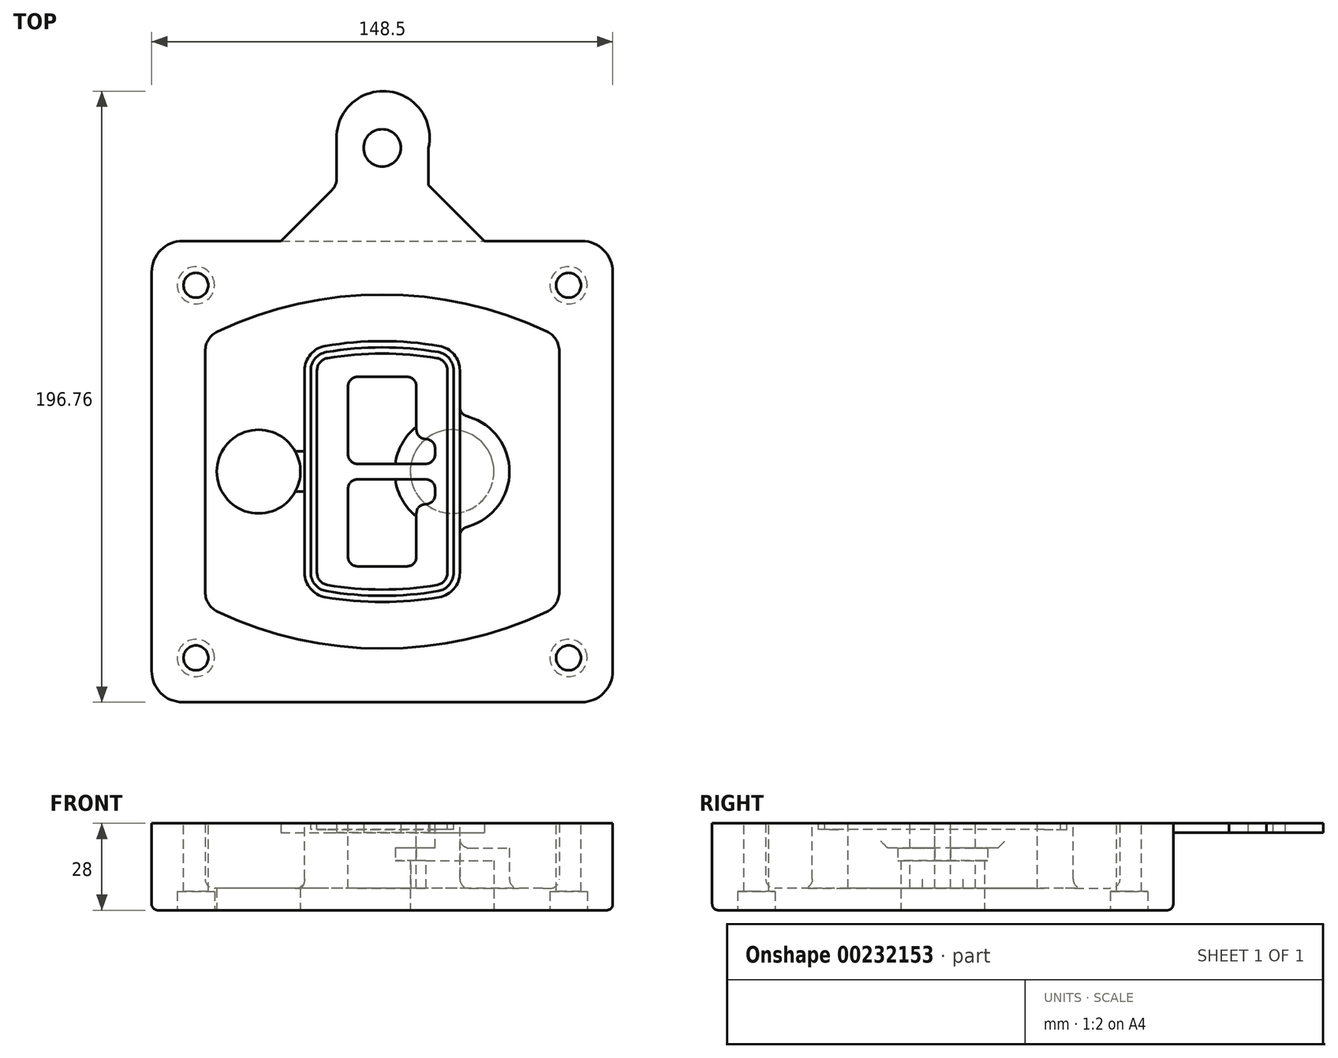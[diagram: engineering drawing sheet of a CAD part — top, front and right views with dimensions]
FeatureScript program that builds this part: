
annotation { "Feature Type Name" : "Feature", "Feature Type Description" : "" }
export const myFeature = defineFeature(function(context is Context, id is Id, definition is map)
    precondition{}
    {
        {
            var Q0;
            Q0=qCreatedBy(makeId("Top.planeOp"),FACE);
            var sketch = newSketch(context, id + "F0", { "sketchPlane" : qUnion([Q0])});
            skPoint(sketch, "E0.rect.middle", {"position": v(0, 0) * mm});
            skLineSegment(sketch, "E1.bottom", {"start": v(-64.25, -74.25) * mm, "end": v(64.25, -74.25) * mm});
            skLineSegment(sketch, "E1.top", {"start": v(-64.25, 74.25) * mm, "end": v(64.25, 74.25) * mm});
            skLineSegment(sketch, "E1.left", {"start": v(-74.25, -64.25) * mm, "end": v(-74.25, 64.25) * mm});
            skLineSegment(sketch, "E1.right", {"start": v(74.25, -64.25) * mm, "end": v(74.25, 64.25) * mm});
            skLineSegment(sketch, "E2", {"start": v(-74.25, 74.25) * mm, "end": v(74.25, -74.25) * mm, "construction": true});
            skLineSegment(sketch, "E3", {"start": v(74.25, 74.25) * mm, "end": v(-74.25, -74.25) * mm, "construction": true});
            skCircle(sketch, "E4", {"center": v(-60, 60) * mm, "radius": 4 * mm});
            skCircle(sketch, "E5", {"center": v(60, 60) * mm, "radius": 4 * mm});
            skCircle(sketch, "E6", {"center": v(60, -60) * mm, "radius": 4 * mm});
            skCircle(sketch, "E7", {"center": v(-60, -60) * mm, "radius": 4 * mm});
            skLineSegment(sketch, "E8", {"start": v(-60, 60) * mm, "end": v(60, 60) * mm, "construction": true});
            skLineSegment(sketch, "E9", {"start": v(60, 60) * mm, "end": v(60, -60) * mm, "construction": true});
            skLineSegment(sketch, "E10", {"start": v(60, -60) * mm, "end": v(-60, -60) * mm, "construction": true});
            skLineSegment(sketch, "E11", {"start": v(-60, -60) * mm, "end": v(-60, 60) * mm, "construction": true});
            skLineSegment(sketch, "E12", {"start": v(-60, 38.83) * mm, "end": v(-60, -38.83) * mm});
            skLineSegment(sketch, "E13", {"start": v(60, 38.83) * mm, "end": v(60, -38.83) * mm});
            skArc(sketch, "E14", {"start": v(54.26, 47.88) * mm, "mid": v(0, 60) * mm, "end": v(-54.26, 47.88) * mm});
            skArc(sketch, "E15", {"start": v(-54.26, -47.88) * mm, "mid": v(0, -60) * mm, "end": v(54.26, -47.88) * mm});
            skLineSegment(sketch, "E16", {"start": v(-60, 0) * mm, "end": v(60, 0) * mm, "construction": true});
            skPoint(sketch, "E17.visualSharp", {"position": v(-60, -45) * mm});
            skArc(sketch, "E17.filletArc", {"start": v(-60, -38.83) * mm, "mid": v(-58.44, -44.2) * mm, "end": v(-54.26, -47.88) * mm});
            skPoint(sketch, "E18.visualSharp", {"position": v(-60, 45) * mm});
            skArc(sketch, "E18.filletArc", {"start": v(-54.26, 47.88) * mm, "mid": v(-58.44, 44.2) * mm, "end": v(-60, 38.83) * mm});
            skPoint(sketch, "E19.visualSharp", {"position": v(60, 45) * mm});
            skArc(sketch, "E19.filletArc", {"start": v(60, 38.83) * mm, "mid": v(58.44, 44.2) * mm, "end": v(54.26, 47.88) * mm});
            skPoint(sketch, "E20.visualSharp", {"position": v(60, -45) * mm});
            skArc(sketch, "E20.filletArc", {"start": v(54.26, -47.88) * mm, "mid": v(58.44, -44.2) * mm, "end": v(60, -38.83) * mm});
            skPoint(sketch, "E21.visualSharp", {"position": v(-74.25, 74.25) * mm});
            skArc(sketch, "E21.filletArc", {"start": v(-64.25, 74.25) * mm, "mid": v(-71.32, 71.32) * mm, "end": v(-74.25, 64.25) * mm});
            skPoint(sketch, "E22.visualSharp", {"position": v(74.25, 74.25) * mm});
            skArc(sketch, "E22.filletArc", {"start": v(74.25, 64.25) * mm, "mid": v(71.32, 71.32) * mm, "end": v(64.25, 74.25) * mm});
            skPoint(sketch, "E23.visualSharp", {"position": v(74.25, -74.25) * mm});
            skArc(sketch, "E23.filletArc", {"start": v(64.25, -74.25) * mm, "mid": v(71.32, -71.32) * mm, "end": v(74.25, -64.25) * mm});
            skPoint(sketch, "E24.visualSharp", {"position": v(-74.25, -74.25) * mm});
            skArc(sketch, "E24.filletArc", {"start": v(-74.25, -64.25) * mm, "mid": v(-71.32, -71.32) * mm, "end": v(-64.25, -74.25) * mm});
            skArc(sketch, "E25.0", {"start": v(57, 38.83) * mm, "mid": v(55.9, 42.58) * mm, "end": v(52.98, 45.17) * mm});
            skLineSegment(sketch, "E25.1", {"start": v(57, 38.83) * mm, "end": v(57, -38.83) * mm});
            skArc(sketch, "E25.2", {"start": v(52.98, -45.17) * mm, "mid": v(55.9, -42.58) * mm, "end": v(57, -38.83) * mm});
            skArc(sketch, "E25.3", {"start": v(-52.98, -45.17) * mm, "mid": v(0, -57) * mm, "end": v(52.98, -45.17) * mm});
            skArc(sketch, "E25.4", {"start": v(-57, -38.83) * mm, "mid": v(-55.9, -42.58) * mm, "end": v(-52.98, -45.17) * mm});
            skArc(sketch, "E25.5", {"start": v(52.98, 45.17) * mm, "mid": v(0, 57) * mm, "end": v(-52.98, 45.17) * mm});
            skLineSegment(sketch, "E25.6", {"start": v(-57, 38.83) * mm, "end": v(-57, -38.83) * mm});
            skArc(sketch, "E25.7", {"start": v(-52.98, 45.17) * mm, "mid": v(-55.9, 42.58) * mm, "end": v(-57, 38.83) * mm});
            skArc(sketch, "E26.0", {"start": v(-55.96, 51.5) * mm, "mid": v(-61.82, 46.33) * mm, "end": v(-64, 38.83) * mm});
            skArc(sketch, "E26.1", {"start": v(55.96, 51.5) * mm, "mid": v(0, 64) * mm, "end": v(-55.96, 51.5) * mm});
            skArc(sketch, "E26.2", {"start": v(64, 38.83) * mm, "mid": v(61.82, 46.33) * mm, "end": v(55.96, 51.5) * mm});
            skLineSegment(sketch, "E26.3", {"start": v(64, 38.83) * mm, "end": v(64, -38.83) * mm});
            skArc(sketch, "E26.4", {"start": v(55.96, -51.5) * mm, "mid": v(61.82, -46.33) * mm, "end": v(64, -38.83) * mm});
            skLineSegment(sketch, "E26.5", {"start": v(-64, 38.83) * mm, "end": v(-64, -38.83) * mm});
            skArc(sketch, "E26.6", {"start": v(-55.96, -51.5) * mm, "mid": v(0, -64) * mm, "end": v(55.96, -51.5) * mm});
            skArc(sketch, "E26.7", {"start": v(-64, -38.83) * mm, "mid": v(-61.82, -46.33) * mm, "end": v(-55.96, -51.5) * mm});
            skSolve(sketch);
        }
        {
            var Q0;
            Q0=makeQuery(id+"F0.imprint","IMPRINT",FACE,{"disambiguationData":[TD([[makeQuery(id+"F0.imprint","IMPRINT",EDGE,{"derivedFrom":sQuery(id+"F0.wireOp",EDGE,"E1.bottom")}),1.0]])]});
            var Q1;
            Q1=makeQuery(id+"F0.imprint","IMPRINT",FACE,{"disambiguationData":[TD([[makeQuery(id+"F0.imprint","IMPRINT",EDGE,{"derivedFrom":sQuery(id+"F0.wireOp",EDGE,"E12")}),1.0]])]});
            var Q2;
            Q2=makeQuery(id+"F0.imprint","IMPRINT",FACE,{"disambiguationData":[TD([[makeQuery(id+"F0.imprint","IMPRINT",EDGE,{"derivedFrom":sQuery(id+"F0.wireOp",EDGE,"E25.0")}),1.0]])]});
            var Q3;
            Q3=makeQuery(id+"F0.imprint","IMPRINT",FACE,{"disambiguationData":[TD([[makeQuery(id+"F0.imprint","IMPRINT",EDGE,{"derivedFrom":sQuery(id+"F0.wireOp",EDGE,"E12")}),-1.0]])]});
            extrude(context, id + "F1", {"entities" : qUnion([Q0, Q1, Q2, Q3]), "oppositeDirection" : true, "depth" : 25 * mm});
        }
        {
            var Q0;
            Q0=makeQuery(id+"F0.imprint","IMPRINT",FACE,{"disambiguationData":[TD([[makeQuery(id+"F0.imprint","IMPRINT",EDGE,{"derivedFrom":sQuery(id+"F0.wireOp",EDGE,"E12")}),1.0]])]});
            extrude(context, id + "F2", {"entities" : qUnion([Q0]), "operationType" : NewBodyOperationType.ADD, "depth" : 3 * mm});
        }
        {
            var Q0;
            Q0=makeQuery(id+"F0.imprint","IMPRINT",FACE,{"disambiguationData":[TD([[makeQuery(id+"F0.imprint","IMPRINT",EDGE,{"derivedFrom":sQuery(id+"F0.wireOp",EDGE,"E25.0")}),1.0]])]});
            extrude(context, id + "F3", {"entities" : qUnion([Q0]), "operationType" : NewBodyOperationType.REMOVE, "oppositeDirection" : true, "depth" : 18 * mm});
        }
        {
            var Q0;
            Q0=makeQuery(id+"F2.opExtrude","CAP_FACE",FACE,{"disambiguationData":[OSD([sQuery(id+"F0.wireOp",EDGE,"E12"),sQuery(id+"F0.wireOp",EDGE,"E13"),sQuery(id+"F0.wireOp",EDGE,"E14"),sQuery(id+"F0.wireOp",EDGE,"E15"),sQuery(id+"F0.wireOp",EDGE,"E17.filletArc"),sQuery(id+"F0.wireOp",EDGE,"E18.filletArc"),sQuery(id+"F0.wireOp",EDGE,"E19.filletArc"),sQuery(id+"F0.wireOp",EDGE,"E20.filletArc"),sQuery(id+"F0.wireOp",EDGE,"E25.0"),sQuery(id+"F0.wireOp",EDGE,"E25.1"),sQuery(id+"F0.wireOp",EDGE,"E25.2"),sQuery(id+"F0.wireOp",EDGE,"E25.3"),sQuery(id+"F0.wireOp",EDGE,"E25.4"),sQuery(id+"F0.wireOp",EDGE,"E25.5"),sQuery(id+"F0.wireOp",EDGE,"E25.6"),sQuery(id+"F0.wireOp",EDGE,"E25.7")])],"isStart":false});
            var sketch = newSketch(context, id + "F4", { "sketchPlane" : qUnion([Q0])});
            skArc(sketch, "E27.0", {"start": v(-18.34, -40.45) * mm, "mid": v(0, -42) * mm, "end": v(18.34, -40.45) * mm});
            skArc(sketch, "E28.0", {"start": v(18.34, 40.45) * mm, "mid": v(0, 42) * mm, "end": v(-18.34, 40.45) * mm});
            skLineSegment(sketch, "E29", {"start": v(-25, 32.57) * mm, "end": v(-25, -32.57) * mm});
            skLineSegment(sketch, "E30", {"start": v(25, 32.57) * mm, "end": v(25, -32.57) * mm});
            skLineSegment(sketch, "E31", {"start": v(-25, 39.1) * mm, "end": v(25, 39.1) * mm, "construction": true});
            skLineSegment(sketch, "E32", {"start": v(-25, -39.1) * mm, "end": v(25, -39.1) * mm, "construction": true});
            skPoint(sketch, "E33.visualSharp", {"position": v(-25, 39.1) * mm});
            skArc(sketch, "E33.filletArc", {"start": v(-18.34, 40.45) * mm, "mid": v(-23.11, 37.73) * mm, "end": v(-25, 32.57) * mm});
            skPoint(sketch, "E34.visualSharp", {"position": v(25, 39.1) * mm});
            skArc(sketch, "E34.filletArc", {"start": v(25, 32.57) * mm, "mid": v(23.11, 37.73) * mm, "end": v(18.34, 40.45) * mm});
            skPoint(sketch, "E35.visualSharp", {"position": v(25, -39.1) * mm});
            skArc(sketch, "E35.filletArc", {"start": v(18.34, -40.45) * mm, "mid": v(23.11, -37.73) * mm, "end": v(25, -32.57) * mm});
            skPoint(sketch, "E36.visualSharp", {"position": v(-25, -39.1) * mm});
            skArc(sketch, "E36.filletArc", {"start": v(-25, -32.57) * mm, "mid": v(-23.11, -37.73) * mm, "end": v(-18.34, -40.45) * mm});
            skArc(sketch, "E37.0", {"start": v(52.98, 45.17) * mm, "mid": v(0, 57) * mm, "end": v(-52.98, 45.17) * mm});
            skArc(sketch, "E37.1", {"start": v(-52.98, 45.17) * mm, "mid": v(-55.9, 42.58) * mm, "end": v(-57, 38.83) * mm});
            skLineSegment(sketch, "E37.2", {"start": v(-57, 38.83) * mm, "end": v(-57, -38.83) * mm});
            skArc(sketch, "E37.3", {"start": v(-57, -38.83) * mm, "mid": v(-55.9, -42.58) * mm, "end": v(-52.98, -45.17) * mm});
            skArc(sketch, "E37.4", {"start": v(-52.98, -45.17) * mm, "mid": v(0, -57) * mm, "end": v(52.98, -45.17) * mm});
            skArc(sketch, "E37.5", {"start": v(52.98, -45.17) * mm, "mid": v(55.9, -42.58) * mm, "end": v(57, -38.83) * mm});
            skLineSegment(sketch, "E37.6", {"start": v(57, 38.83) * mm, "end": v(57, -38.83) * mm});
            skArc(sketch, "E37.7", {"start": v(57, 38.83) * mm, "mid": v(55.9, 42.58) * mm, "end": v(52.98, 45.17) * mm});
            skLineSegment(sketch, "E38.0", {"start": v(23, 32.57) * mm, "end": v(23, -32.57) * mm});
            skArc(sketch, "E38.1", {"start": v(18, -38.48) * mm, "mid": v(21.58, -36.44) * mm, "end": v(23, -32.57) * mm});
            skArc(sketch, "E38.2", {"start": v(-18, -38.48) * mm, "mid": v(0, -40) * mm, "end": v(18, -38.48) * mm});
            skArc(sketch, "E38.3", {"start": v(-23, -32.57) * mm, "mid": v(-21.58, -36.44) * mm, "end": v(-18, -38.48) * mm});
            skLineSegment(sketch, "E38.4", {"start": v(-23, 32.57) * mm, "end": v(-23, -32.57) * mm});
            skArc(sketch, "E38.5", {"start": v(23, 32.57) * mm, "mid": v(21.58, 36.44) * mm, "end": v(18, 38.48) * mm});
            skArc(sketch, "E38.6", {"start": v(-18, 38.48) * mm, "mid": v(-21.58, 36.44) * mm, "end": v(-23, 32.57) * mm});
            skArc(sketch, "E38.7", {"start": v(18, 38.48) * mm, "mid": v(0, 40) * mm, "end": v(-18, 38.48) * mm});
            skArc(sketch, "E39.0", {"start": v(21, 32.57) * mm, "mid": v(20.06, 35.15) * mm, "end": v(17.67, 36.5) * mm});
            skLineSegment(sketch, "E39.1", {"start": v(21, 32.57) * mm, "end": v(21, -32.57) * mm});
            skArc(sketch, "E39.2", {"start": v(17.67, -36.5) * mm, "mid": v(20.06, -35.15) * mm, "end": v(21, -32.57) * mm});
            skArc(sketch, "E39.3", {"start": v(-17.67, -36.5) * mm, "mid": v(0, -38) * mm, "end": v(17.67, -36.5) * mm});
            skArc(sketch, "E39.4", {"start": v(-21, -32.57) * mm, "mid": v(-20.06, -35.15) * mm, "end": v(-17.67, -36.5) * mm});
            skArc(sketch, "E39.5", {"start": v(17.67, 36.5) * mm, "mid": v(0, 38) * mm, "end": v(-17.67, 36.5) * mm});
            skLineSegment(sketch, "E39.6", {"start": v(-21, 32.57) * mm, "end": v(-21, -32.57) * mm});
            skArc(sketch, "E39.7", {"start": v(-17.67, 36.5) * mm, "mid": v(-20.06, 35.15) * mm, "end": v(-21, 32.57) * mm});
            skLineSegment(sketch, "E40", {"start": v(-25, 0) * mm, "end": v(25, 0) * mm, "construction": true});
            skLineSegment(sketch, "E41", {"start": v(-11, 5.5) * mm, "end": v(-11, 27.5) * mm});
            skLineSegment(sketch, "E42", {"start": v(-8, 30.5) * mm, "end": v(8, 30.5) * mm});
            skLineSegment(sketch, "E43", {"start": v(11, 27.5) * mm, "end": v(11, 13.5) * mm});
            skLineSegment(sketch, "E44", {"start": v(14, 10.5) * mm, "end": v(14, 10.5) * mm});
            skLineSegment(sketch, "E45", {"start": v(17, 7.5) * mm, "end": v(17, 5.5) * mm});
            skLineSegment(sketch, "E46", {"start": v(14, 2.5) * mm, "end": v(-8, 2.5) * mm});
            skPoint(sketch, "E47.visualSharp", {"position": v(-11, 30.5) * mm});
            skArc(sketch, "E47.filletArc", {"start": v(-8, 30.5) * mm, "mid": v(-10.12, 29.62) * mm, "end": v(-11, 27.5) * mm});
            skPoint(sketch, "E48.visualSharp", {"position": v(11, 30.5) * mm});
            skArc(sketch, "E48.filletArc", {"start": v(11, 27.5) * mm, "mid": v(10.12, 29.62) * mm, "end": v(8, 30.5) * mm});
            skPoint(sketch, "E49.visualSharp", {"position": v(11, 10.5) * mm});
            skArc(sketch, "E49.filletArc", {"start": v(11, 13.5) * mm, "mid": v(11.88, 11.38) * mm, "end": v(14, 10.5) * mm});
            skPoint(sketch, "E50.visualSharp", {"position": v(17, 10.5) * mm});
            skArc(sketch, "E50.filletArc", {"start": v(17, 7.5) * mm, "mid": v(16.12, 9.62) * mm, "end": v(14, 10.5) * mm});
            skPoint(sketch, "E51.visualSharp", {"position": v(17, 2.5) * mm});
            skArc(sketch, "E51.filletArc", {"start": v(14, 2.5) * mm, "mid": v(16.12, 3.38) * mm, "end": v(17, 5.5) * mm});
            skPoint(sketch, "E52.visualSharp", {"position": v(-11, 2.5) * mm});
            skArc(sketch, "E52.filletArc", {"start": v(-11, 5.5) * mm, "mid": v(-10.12, 3.38) * mm, "end": v(-8, 2.5) * mm});
            skLineSegment(sketch, "E53.0.MirrorCS", {"start": v(14, -2.5) * mm, "end": v(-8, -2.5) * mm});
            skArc(sketch, "E54.0.MirrorCS", {"start": v(-11, -5.5) * mm, "mid": v(-10.12, -3.38) * mm, "end": v(-8, -2.5) * mm});
            skLineSegment(sketch, "E55.0.MirrorCS", {"start": v(-11, -5.5) * mm, "end": v(-11, -27.5) * mm});
            skArc(sketch, "E56.0.MirrorCS", {"start": v(-8, -30.5) * mm, "mid": v(-10.12, -29.62) * mm, "end": v(-11, -27.5) * mm});
            skLineSegment(sketch, "E57.0.MirrorCS", {"start": v(-8, -30.5) * mm, "end": v(8, -30.5) * mm});
            skArc(sketch, "E58.0.MirrorCS", {"start": v(11, -27.5) * mm, "mid": v(10.12, -29.62) * mm, "end": v(8, -30.5) * mm});
            skLineSegment(sketch, "E59.0.MirrorCS", {"start": v(11, -27.5) * mm, "end": v(11, -13.5) * mm});
            skArc(sketch, "E60.0.MirrorCS", {"start": v(11, -13.5) * mm, "mid": v(11.88, -11.38) * mm, "end": v(14, -10.5) * mm});
            skArc(sketch, "E61.0.MirrorCS", {"start": v(17, -7.5) * mm, "mid": v(16.12, -9.62) * mm, "end": v(14, -10.5) * mm});
            skLineSegment(sketch, "E62.0.MirrorCS", {"start": v(17, -7.5) * mm, "end": v(17, -5.5) * mm});
            skArc(sketch, "E63.0.MirrorCS", {"start": v(14, -2.5) * mm, "mid": v(16.12, -3.38) * mm, "end": v(17, -5.5) * mm});
            skSolve(sketch);
        }
        {
            var Q0;
            Q0=makeQuery(id+"F4.imprint","IMPRINT",FACE,{"disambiguationData":[TD([[makeQuery(id+"F4.imprint","IMPRINT",EDGE,{"derivedFrom":sQuery(id+"F4.wireOp",EDGE,"E27.0")}),1.0]])]});
            var Q1;
            Q1=makeQuery(id+"F4.imprint","IMPRINT",FACE,{"disambiguationData":[TD([[makeQuery(id+"F4.imprint","IMPRINT",EDGE,{"derivedFrom":sQuery(id+"F4.wireOp",EDGE,"E38.0")}),-1.0]])]});
            var Q2;
            Q2=makeQuery(id+"F4.imprint","IMPRINT",FACE,{"disambiguationData":[TD([[makeQuery(id+"F4.imprint","IMPRINT",EDGE,{"derivedFrom":sQuery(id+"F4.wireOp",EDGE,"E39.0")}),1.0]])]});
            extrude(context, id + "F5", {"entities" : qUnion([Q0, Q1, Q2]), "operationType" : NewBodyOperationType.ADD, "endBound" : BoundingType.UP_TO_NEXT, "oppositeDirection" : true, "depth" : 25 * mm});
        }
        {
            var Q0;
            Q0=makeQuery(id+"F4.imprint","IMPRINT",FACE,{"disambiguationData":[TD([[makeQuery(id+"F4.imprint","IMPRINT",EDGE,{"derivedFrom":sQuery(id+"F4.wireOp",EDGE,"E38.0")}),-1.0]])]});
            extrude(context, id + "F6", {"entities" : qUnion([Q0]), "operationType" : NewBodyOperationType.REMOVE, "oppositeDirection" : true, "depth" : 2 * mm});
        }
        {
            var Q0;
            Q0=makeQuery(id+"F1.opExtrude","CAP_FACE",FACE,{"disambiguationData":[OSD([sQuery(id+"F0.wireOp",EDGE,"E1.bottom"),sQuery(id+"F0.wireOp",EDGE,"E1.top"),sQuery(id+"F0.wireOp",EDGE,"E1.left"),sQuery(id+"F0.wireOp",EDGE,"E1.right"),sQuery(id+"F0.wireOp",EDGE,"E4"),sQuery(id+"F0.wireOp",EDGE,"E5"),sQuery(id+"F0.wireOp",EDGE,"E6"),sQuery(id+"F0.wireOp",EDGE,"E7"),sQuery(id+"F0.wireOp",EDGE,"E21.filletArc"),sQuery(id+"F0.wireOp",EDGE,"E22.filletArc"),sQuery(id+"F0.wireOp",EDGE,"E23.filletArc"),sQuery(id+"F0.wireOp",EDGE,"E24.filletArc")])],"isStart":false});
            var sketch = newSketch(context, id + "F7", { "sketchPlane" : qUnion([Q0])});
            skCircle(sketch, "E64", {"center": v(22.5, 0) * mm, "radius": 13.47 * mm});
            skCircle(sketch, "E65", {"center": v(-39.81, 0) * mm, "radius": 13.47 * mm});
            skLineSegment(sketch, "E66", {"start": v(74.25, 0) * mm, "end": v(-74.25, 0) * mm});
            skCircle(sketch, "E67", {"center": v(22.5, 0) * mm, "radius": 18.47 * mm});
            skCircle(sketch, "E68", {"center": v(60, -60) * mm, "radius": 6 * mm});
            skCircle(sketch, "E69", {"center": v(-60, -60) * mm, "radius": 6 * mm});
            skCircle(sketch, "E70", {"center": v(-60, 60) * mm, "radius": 6 * mm});
            skCircle(sketch, "E71", {"center": v(60, 60) * mm, "radius": 6 * mm});
            skSolve(sketch);
        }
        {
            var Q0;
            {var subQ1=sQuery(id+"F7.wireOp",EDGE,"E66");var subQ4=sQuery(id+"F7.wireOp",EDGE,"E64");var subQ6=makeQuery(id+"F7.imprint","INTERSECT",VERTEX,{"disambiguationData":[OD(0.0)],"derivedFrom":[subQ4,subQ1]});Q0=makeQuery(id+"F7.imprint","IMPRINT",FACE,{"disambiguationData":[TD([[makeQuery(id+"F7.imprint","IMPRINT",EDGE,{"disambiguationData":[TD([[subQ6,-1.0]])],"derivedFrom":subQ4}),-1.0]])]});}
            var Q1;
            {var subQ0=sQuery(id+"F7.wireOp",EDGE,"E66");var subQ1=sQuery(id+"F7.wireOp",EDGE,"E64");var subQ3=makeQuery(id+"F7.imprint","INTERSECT",VERTEX,{"disambiguationData":[OD(0.0)],"derivedFrom":[subQ1,subQ0]});Q1=makeQuery(id+"F7.imprint","IMPRINT",FACE,{"disambiguationData":[TD([[makeQuery(id+"F7.imprint","IMPRINT",EDGE,{"disambiguationData":[TD([[subQ3,-1.0]])],"derivedFrom":subQ1}),1.0]])]});}
            var Q2;
            {var subQ0=sQuery(id+"F7.wireOp",EDGE,"E66");var subQ1=sQuery(id+"F7.wireOp",EDGE,"E64");var subQ3=makeQuery(id+"F7.imprint","INTERSECT",VERTEX,{"disambiguationData":[OD(0.0)],"derivedFrom":[subQ1,subQ0]});Q2=makeQuery(id+"F7.imprint","IMPRINT",FACE,{"disambiguationData":[TD([[makeQuery(id+"F7.imprint","IMPRINT",EDGE,{"disambiguationData":[TD([[subQ3,1.0]])],"derivedFrom":subQ1}),1.0]])]});}
            var Q3;
            {var subQ1=sQuery(id+"F7.wireOp",EDGE,"E66");var subQ4=sQuery(id+"F7.wireOp",EDGE,"E64");var subQ6=makeQuery(id+"F7.imprint","INTERSECT",VERTEX,{"disambiguationData":[OD(0.0)],"derivedFrom":[subQ4,subQ1]});Q3=makeQuery(id+"F7.imprint","IMPRINT",FACE,{"disambiguationData":[TD([[makeQuery(id+"F7.imprint","IMPRINT",EDGE,{"disambiguationData":[TD([[subQ6,1.0]])],"derivedFrom":subQ4}),-1.0]])]});}
            extrude(context, id + "F8", {"entities" : qUnion([Q0, Q1, Q2, Q3]), "operationType" : NewBodyOperationType.ADD, "oppositeDirection" : true, "depth" : 20 * mm});
        }
        {
            var Q0;
            {var subQ0=sQuery(id+"F7.wireOp",EDGE,"E66");var subQ1=sQuery(id+"F7.wireOp",EDGE,"E64");var subQ3=makeQuery(id+"F7.imprint","INTERSECT",VERTEX,{"disambiguationData":[OD(0.0)],"derivedFrom":[subQ1,subQ0]});Q0=makeQuery(id+"F7.imprint","IMPRINT",FACE,{"disambiguationData":[TD([[makeQuery(id+"F7.imprint","IMPRINT",EDGE,{"disambiguationData":[TD([[subQ3,-1.0]])],"derivedFrom":subQ1}),1.0]])]});}
            var Q1;
            {var subQ0=sQuery(id+"F7.wireOp",EDGE,"E66");var subQ1=sQuery(id+"F7.wireOp",EDGE,"E64");var subQ3=makeQuery(id+"F7.imprint","INTERSECT",VERTEX,{"disambiguationData":[OD(0.0)],"derivedFrom":[subQ1,subQ0]});Q1=makeQuery(id+"F7.imprint","IMPRINT",FACE,{"disambiguationData":[TD([[makeQuery(id+"F7.imprint","IMPRINT",EDGE,{"disambiguationData":[TD([[subQ3,1.0]])],"derivedFrom":subQ1}),1.0]])]});}
            extrude(context, id + "F9", {"entities" : qUnion([Q0, Q1]), "operationType" : NewBodyOperationType.REMOVE, "oppositeDirection" : true, "depth" : 16 * mm});
        }
        {
            var Q0;
            {var subQ0=sQuery(id+"F7.wireOp",EDGE,"E66");var subQ1=sQuery(id+"F7.wireOp",EDGE,"E65");var subQ3=makeQuery(id+"F7.imprint","INTERSECT",VERTEX,{"disambiguationData":[OD(0.0)],"derivedFrom":[subQ1,subQ0]});Q0=makeQuery(id+"F7.imprint","IMPRINT",FACE,{"disambiguationData":[TD([[makeQuery(id+"F7.imprint","IMPRINT",EDGE,{"disambiguationData":[TD([[subQ3,-1.0]])],"derivedFrom":subQ1}),1.0]])]});}
            var Q1;
            {var subQ0=sQuery(id+"F7.wireOp",EDGE,"E66");var subQ1=sQuery(id+"F7.wireOp",EDGE,"E65");var subQ3=makeQuery(id+"F7.imprint","INTERSECT",VERTEX,{"disambiguationData":[OD(0.0)],"derivedFrom":[subQ1,subQ0]});Q1=makeQuery(id+"F7.imprint","IMPRINT",FACE,{"disambiguationData":[TD([[makeQuery(id+"F7.imprint","IMPRINT",EDGE,{"disambiguationData":[TD([[subQ3,1.0]])],"derivedFrom":subQ1}),1.0]])]});}
            extrude(context, id + "F10", {"entities" : qUnion([Q0, Q1]), "operationType" : NewBodyOperationType.REMOVE, "oppositeDirection" : true, "depth" : 25 * mm});
        }
        {
            var Q0;
            Q0=makeQuery(id+"F7.imprint","IMPRINT",FACE,{"disambiguationData":[TD([[makeQuery(id+"F7.imprint","IMPRINT",EDGE,{"derivedFrom":sQuery(id+"F7.wireOp",EDGE,"E68")}),1.0]])]});
            var Q1;
            Q1=makeQuery(id+"F7.imprint","IMPRINT",FACE,{"disambiguationData":[TD([[makeQuery(id+"F7.imprint","IMPRINT",EDGE,{"derivedFrom":makeQuery(id+"F1.opExtrude","CAP_EDGE",EDGE,{"disambiguationData":[OSD([sQuery(id+"F0.wireOp",EDGE,"E5")])],"isStart":false})}),-1.0]])]});
            var Q2;
            Q2=makeQuery(id+"F7.imprint","IMPRINT",FACE,{"disambiguationData":[TD([[makeQuery(id+"F7.imprint","IMPRINT",EDGE,{"derivedFrom":sQuery(id+"F7.wireOp",EDGE,"E69")}),1.0]])]});
            var Q3;
            Q3=makeQuery(id+"F7.imprint","IMPRINT",FACE,{"disambiguationData":[TD([[makeQuery(id+"F7.imprint","IMPRINT",EDGE,{"derivedFrom":makeQuery(id+"F1.opExtrude","CAP_EDGE",EDGE,{"disambiguationData":[OSD([sQuery(id+"F0.wireOp",EDGE,"E4")])],"isStart":false})}),-1.0]])]});
            var Q4;
            Q4=makeQuery(id+"F7.imprint","IMPRINT",FACE,{"disambiguationData":[TD([[makeQuery(id+"F7.imprint","IMPRINT",EDGE,{"derivedFrom":sQuery(id+"F7.wireOp",EDGE,"E70")}),1.0]])]});
            var Q5;
            Q5=makeQuery(id+"F7.imprint","IMPRINT",FACE,{"disambiguationData":[TD([[makeQuery(id+"F7.imprint","IMPRINT",EDGE,{"derivedFrom":makeQuery(id+"F1.opExtrude","CAP_EDGE",EDGE,{"disambiguationData":[OSD([sQuery(id+"F0.wireOp",EDGE,"E7")])],"isStart":false})}),-1.0]])]});
            var Q6;
            Q6=makeQuery(id+"F7.imprint","IMPRINT",FACE,{"disambiguationData":[TD([[makeQuery(id+"F7.imprint","IMPRINT",EDGE,{"derivedFrom":sQuery(id+"F7.wireOp",EDGE,"E71")}),1.0]])]});
            var Q7;
            Q7=makeQuery(id+"F7.imprint","IMPRINT",FACE,{"disambiguationData":[TD([[makeQuery(id+"F7.imprint","IMPRINT",EDGE,{"derivedFrom":makeQuery(id+"F1.opExtrude","CAP_EDGE",EDGE,{"disambiguationData":[OSD([sQuery(id+"F0.wireOp",EDGE,"E6")])],"isStart":false})}),-1.0]])]});
            extrude(context, id + "F11", {"entities" : qUnion([Q0, Q1, Q2, Q3, Q4, Q5, Q6, Q7]), "operationType" : NewBodyOperationType.REMOVE, "oppositeDirection" : true, "depth" : 6 * mm});
        }
        {
            var Q0;
            Q0=makeQuery(id+"F9.boolean.opBoolean","COPY",FACE,{"derivedFrom":makeQuery(id+"F9.opExtrude","CAP_FACE",FACE,{"disambiguationData":[OSD([sQuery(id+"F7.wireOp",EDGE,"E64")])],"isStart":false})});
            var sketch = newSketch(context, id + "F12", { "sketchPlane" : qUnion([Q0])});
            skArc(sketch, "E72.0", {"start": v(11, 14.45) * mm, "mid": v(6.45, 9.13) * mm, "end": v(4.2, 2.5) * mm});
            skArc(sketch, "E72.1", {"start": v(4.2, -2.5) * mm, "mid": v(6.45, -9.13) * mm, "end": v(11, -14.45) * mm});
            skLineSegment(sketch, "E73", {"start": v(4.2, -2.5) * mm, "end": v(14, -2.5) * mm});
            skLineSegment(sketch, "E74.0", {"start": v(14, 2.5) * mm, "end": v(4.2, 2.5) * mm});
            skArc(sketch, "E74.1", {"start": v(14, 2.5) * mm, "mid": v(16.12, 3.38) * mm, "end": v(17, 5.5) * mm});
            skLineSegment(sketch, "E74.2", {"start": v(17, 7.5) * mm, "end": v(17, 5.5) * mm});
            skArc(sketch, "E74.3", {"start": v(17, 7.5) * mm, "mid": v(16.12, 9.62) * mm, "end": v(14, 10.5) * mm});
            skArc(sketch, "E74.4", {"start": v(11, 13.5) * mm, "mid": v(11.88, 11.38) * mm, "end": v(14, 10.5) * mm});
            skLineSegment(sketch, "E74.5", {"start": v(11, 14.45) * mm, "end": v(11, 13.5) * mm});
            skLineSegment(sketch, "E74.7", {"start": v(14, -2.5) * mm, "end": v(4.2, -2.5) * mm});
            skArc(sketch, "E74.8", {"start": v(14, -2.5) * mm, "mid": v(16.12, -3.38) * mm, "end": v(17, -5.5) * mm});
            skLineSegment(sketch, "E74.9", {"start": v(17, -7.5) * mm, "end": v(17, -5.5) * mm});
            skArc(sketch, "E74.10", {"start": v(17, -7.5) * mm, "mid": v(16.12, -9.62) * mm, "end": v(14, -10.5) * mm});
            skArc(sketch, "E74.11", {"start": v(11, -13.5) * mm, "mid": v(11.88, -11.38) * mm, "end": v(14, -10.5) * mm});
            skLineSegment(sketch, "E74.12", {"start": v(11, -14.45) * mm, "end": v(11, -13.5) * mm});
            skPoint(sketch, "E75.orphan", {"position": v(11, -27.5) * mm});
            skPoint(sketch, "E76.orphan", {"position": v(-8, -2.5) * mm});
            skPoint(sketch, "E77.orphan", {"position": v(-8, 2.5) * mm});
            skPoint(sketch, "E78.orphan", {"position": v(11, 27.5) * mm});
            skSolve(sketch);
        }
        {
            var Q0;
            {var subQ7=sQuery(id+"F12.wireOp",EDGE,"E72.0");var subQ14=sQuery(id+"F12.wireOp",EDGE,"E72.1");var subQ16=sQuery(id+"F12.wireOp",EDGE,"E74.1");var subQ18=sQuery(id+"F12.wireOp",EDGE,"E74.8");Q0=qUnion([makeQuery(id+"F12.imprint","IMPRINT",FACE,{"disambiguationData":[TD([[makeQuery(id+"F12.imprint","IMPRINT",EDGE,{"derivedFrom":subQ7}),1.0]])]}),makeQuery(id+"F12.imprint","IMPRINT",FACE,{"disambiguationData":[TD([[makeQuery(id+"F12.imprint","IMPRINT",EDGE,{"derivedFrom":subQ14}),1.0]])]}),makeQuery(id+"F12.imprint","IMPRINT",FACE,{"disambiguationData":[TD([[makeQuery(id+"F12.imprint","IMPRINT",EDGE,{"derivedFrom":subQ16}),1.0]])]}),makeQuery(id+"F12.imprint","IMPRINT",FACE,{"disambiguationData":[TD([[makeQuery(id+"F12.imprint","IMPRINT",EDGE,{"derivedFrom":subQ18}),-1.0]])]})]);}
            var Q1;
            Q1=makeQuery(id+"F5.boolean.opBoolean","SPLIT",FACE,{"disambiguationData":[TD([makeQuery(id+"F5.opExtrude","SWEPT_FACE",FACE,{"disambiguationData":[OSD([sQuery(id+"F4.wireOp",EDGE,"E41")])]})])],"derivedFrom":makeQuery(id+"F3.boolean.opBoolean","COPY",FACE,{"derivedFrom":makeQuery(id+"F3.opExtrude","CAP_FACE",FACE,{"disambiguationData":[OSD([sQuery(id+"F0.wireOp",EDGE,"E25.0"),sQuery(id+"F0.wireOp",EDGE,"E25.1"),sQuery(id+"F0.wireOp",EDGE,"E25.2"),sQuery(id+"F0.wireOp",EDGE,"E25.3"),sQuery(id+"F0.wireOp",EDGE,"E25.4"),sQuery(id+"F0.wireOp",EDGE,"E25.5"),sQuery(id+"F0.wireOp",EDGE,"E25.6"),sQuery(id+"F0.wireOp",EDGE,"E25.7")])],"isStart":false})})});
            extrude(context, id + "F13", {"entities" : qUnion([Q0]), "operationType" : NewBodyOperationType.REMOVE, "endBound" : BoundingType.UP_TO_SURFACE, "endBoundEntityFace" : qUnion([Q1]), "depth" : 25 * mm});
        }
        {
            var Q0;
            Q0=makeQuery(id+"F3.boolean.opBoolean","COPY",EDGE,{"derivedFrom":makeQuery(id+"F3.opExtrude","CAP_EDGE",EDGE,{"disambiguationData":[OSD([sQuery(id+"F0.wireOp",EDGE,"E25.6")])],"isStart":false})});
            var Q1;
            Q1=makeQuery(id+"F8.boolean.opBoolean","INTERSECT",EDGE,{"derivedFrom":[makeQuery(id+"F5.opExtrude","SWEPT_FACE",FACE,{"disambiguationData":[OSD([sQuery(id+"F4.wireOp",EDGE,"E30")])]}),makeQuery(id+"F8.opExtrude","CAP_FACE",FACE,{"disambiguationData":[OSD([sQuery(id+"F7.wireOp",EDGE,"E67")])],"isStart":false})]});
            var Q2;
            Q2=makeQuery(id+"F8.boolean.opBoolean","INTERSECT",EDGE,{"disambiguationData":[OD(1.0)],"derivedFrom":[makeQuery(id+"F5.opExtrude","SWEPT_FACE",FACE,{"disambiguationData":[OSD([sQuery(id+"F4.wireOp",EDGE,"E30")])]}),makeQuery(id+"F8.opExtrude","SWEPT_FACE",FACE,{"disambiguationData":[OSD([sQuery(id+"F7.wireOp",EDGE,"E67")])]})]});
            var Q3;
            {var subQ0=sQuery(id+"F4.wireOp",EDGE,"E30");Q3=makeQuery(id+"F8.boolean.opBoolean","SPLIT",EDGE,{"disambiguationData":[TD([makeQuery(id+"F5.opExtrude","SWEPT_FACE",FACE,{"disambiguationData":[OSD([sQuery(id+"F4.wireOp",EDGE,"E35.filletArc")])]})])],"derivedFrom":makeQuery(id+"F5.opExtrude","CAP_EDGE",EDGE,{"disambiguationData":[OSD([subQ0])],"isStart":false})});}
            var Q4;
            {var subQ0=sQuery(id+"F0.wireOp",EDGE,"E25.7");var subQ1=sQuery(id+"F0.wireOp",EDGE,"E25.1");var subQ2=sQuery(id+"F0.wireOp",EDGE,"E25.6");var subQ3=sQuery(id+"F0.wireOp",EDGE,"E25.5");var subQ4=sQuery(id+"F0.wireOp",EDGE,"E25.4");var subQ5=sQuery(id+"F0.wireOp",EDGE,"E25.0");var subQ6=sQuery(id+"F0.wireOp",EDGE,"E25.2");var subQ7=sQuery(id+"F0.wireOp",EDGE,"E25.3");Q4=makeQuery(id+"F8.boolean.opBoolean","INTERSECT",EDGE,{"derivedFrom":[makeQuery(id+"F5.boolean.opBoolean","SPLIT",FACE,{"disambiguationData":[TD([makeQuery(id+"F2.opExtrude","SWEPT_FACE",FACE,{"disambiguationData":[OSD([subQ5])]})])],"derivedFrom":makeQuery(id+"F3.boolean.opBoolean","COPY",FACE,{"derivedFrom":makeQuery(id+"F3.opExtrude","CAP_FACE",FACE,{"disambiguationData":[OSD([subQ5,subQ1,subQ6,subQ7,subQ4,subQ3,subQ2,subQ0])],"isStart":false})})}),makeQuery(id+"F8.opExtrude","SWEPT_FACE",FACE,{"disambiguationData":[OSD([sQuery(id+"F7.wireOp",EDGE,"E67")])]})]});}
            var Q5;
            Q5=makeQuery(id+"F8.boolean.opBoolean","INTERSECT",EDGE,{"disambiguationData":[OD(0.0)],"derivedFrom":[makeQuery(id+"F5.opExtrude","SWEPT_FACE",FACE,{"disambiguationData":[OSD([sQuery(id+"F4.wireOp",EDGE,"E30")])]}),makeQuery(id+"F8.opExtrude","SWEPT_FACE",FACE,{"disambiguationData":[OSD([sQuery(id+"F7.wireOp",EDGE,"E67")])]})]});
            fillet(context, id + "F14", {"entities" : qUnion([Q0, Q1, Q2, Q3, Q4, Q5]), "radius" : 3 * mm, "tangentPropagation" : true, "allowEdgeOverflow" : false});
        }
        {
            var Q0;
            Q0=makeQuery(id+"F1.opExtrude","CAP_EDGE",EDGE,{"disambiguationData":[OSD([sQuery(id+"F0.wireOp",EDGE,"E1.bottom")])],"isStart":false});
            fillet(context, id + "F15", {"entities" : qUnion([Q0]), "radius" : 2 * mm, "tangentPropagation" : true, "allowEdgeOverflow" : false});
        }
        {
            var Q0;
            {var subQ0=sQuery(id+"F0.wireOp",EDGE,"E22.filletArc");var subQ1=sQuery(id+"F0.wireOp",EDGE,"E7");var subQ2=sQuery(id+"F0.wireOp",EDGE,"E6");var subQ3=sQuery(id+"F0.wireOp",EDGE,"E5");var subQ4=sQuery(id+"F0.wireOp",EDGE,"E4");var subQ5=sQuery(id+"F0.wireOp",EDGE,"E1.bottom");var subQ6=sQuery(id+"F0.wireOp",EDGE,"E21.filletArc");var subQ7=sQuery(id+"F0.wireOp",EDGE,"E1.top");var subQ8=sQuery(id+"F0.wireOp",EDGE,"E1.left");var subQ9=sQuery(id+"F0.wireOp",EDGE,"E1.right");var subQ10=sQuery(id+"F0.wireOp",EDGE,"E23.filletArc");var subQ11=sQuery(id+"F0.wireOp",EDGE,"E24.filletArc");Q0=makeQuery(id+"F2.boolean.opBoolean","SPLIT",FACE,{"disambiguationData":[TD([makeQuery(id+"F1.opExtrude","SWEPT_FACE",FACE,{"disambiguationData":[OSD([subQ5])]})])],"derivedFrom":makeQuery(id+"F1.opExtrude","CAP_FACE",FACE,{"disambiguationData":[OSD([subQ5,subQ7,subQ8,subQ9,subQ4,subQ3,subQ2,subQ1,subQ6,subQ0,subQ10,subQ11])],"isStart":true})});}
            var sketch = newSketch(context, id + "F16", { "sketchPlane" : qUnion([Q0])});
            skLineSegment(sketch, "E79.0", {"start": v(-64.25, 74.25) * mm, "end": v(64.25, 74.25) * mm});
            skArc(sketch, "E79.1", {"start": v(74.25, 64.25) * mm, "mid": v(71.32, 71.32) * mm, "end": v(64.25, 74.25) * mm});
            skLineSegment(sketch, "E79.2", {"start": v(74.25, -64.25) * mm, "end": v(74.25, 64.25) * mm});
            skArc(sketch, "E79.3", {"start": v(64.25, -74.25) * mm, "mid": v(71.32, -71.32) * mm, "end": v(74.25, -64.25) * mm});
            skLineSegment(sketch, "E79.4", {"start": v(-64.25, -74.25) * mm, "end": v(64.25, -74.25) * mm});
            skArc(sketch, "E79.5", {"start": v(-74.25, -64.25) * mm, "mid": v(-71.32, -71.32) * mm, "end": v(-64.25, -74.25) * mm});
            skLineSegment(sketch, "E79.6", {"start": v(-74.25, -64.25) * mm, "end": v(-74.25, 64.25) * mm});
            skArc(sketch, "E79.7", {"start": v(-64.25, 74.25) * mm, "mid": v(-71.32, 71.32) * mm, "end": v(-74.25, 64.25) * mm});
            skCircle(sketch, "E79.8", {"center": v(-60, -60) * mm, "radius": 4 * mm});
            skCircle(sketch, "E79.10", {"center": v(-60, 60) * mm, "radius": 4 * mm});
            skCircle(sketch, "E79.11", {"center": v(60, 60) * mm, "radius": 4 * mm});
            skCircle(sketch, "E79.12", {"center": v(60, -60) * mm, "radius": 4 * mm});
            skLineSegment(sketch, "E80", {"start": v(0, 74.25) * mm, "end": v(0, 104.25) * mm, "construction": true});
            skCircle(sketch, "E81", {"center": v(0, 104.25) * mm, "radius": 6 * mm});
            skArc(sketch, "E82", {"start": v(14.92, 104.25) * mm, "mid": v(1.32, 122.47) * mm, "end": v(-14.68, 106.32) * mm});
            skLineSegment(sketch, "E83", {"start": v(-32.68, 74.25) * mm, "end": v(-16.14, 90.79) * mm});
            skLineSegment(sketch, "E84", {"start": v(14.92, 92.25) * mm, "end": v(32.92, 74.25) * mm});
            skPoint(sketch, "E85.visualSharp", {"position": v(-14.68, 92.25) * mm});
            skArc(sketch, "E85.filletArc", {"start": v(-16.14, 90.79) * mm, "mid": v(-15.06, 92.4) * mm, "end": v(-14.68, 94.32) * mm});
            skLineSegment(sketch, "E86", {"start": v(-74.25, 0) * mm, "end": v(74.25, 0) * mm, "construction": true});
            skArc(sketch, "E87.MirrorCS", {"start": v(14.92, -104.25) * mm, "mid": v(1.32, -122.47) * mm, "end": v(-14.68, -106.32) * mm});
            skLineSegment(sketch, "E88.MirrorCS", {"start": v(14.92, -104.25) * mm, "end": v(14.92, -92.25) * mm});
            skLineSegment(sketch, "E89.MirrorCS", {"start": v(14.92, -92.25) * mm, "end": v(32.92, -74.25) * mm});
            skLineSegment(sketch, "E90.MirrorCS", {"start": v(0, -74.25) * mm, "end": v(0, -104.25) * mm, "construction": true});
            skCircle(sketch, "E91.MirrorC", {"center": v(0, -104.25) * mm, "radius": 6 * mm});
            skLineSegment(sketch, "E92.MirrorCS", {"start": v(-32.68, -74.25) * mm, "end": v(-16.14, -90.79) * mm});
            skLineSegment(sketch, "E93", {"start": v(-16.14, -90.79) * mm, "end": v(-14.68, -106.32) * mm});
            skLineSegment(sketch, "E94", {"start": v(14.92, 104.25) * mm, "end": v(14.92, 92.25) * mm});
            skLineSegment(sketch, "E95", {"start": v(-14.68, 106.32) * mm, "end": v(-14.68, 94.32) * mm});
            skSolve(sketch);
        }
        {
            var Q0;
            Q0=makeQuery(id+"F16.imprint","IMPRINT",FACE,{"disambiguationData":[TD([[makeQuery(id+"F16.imprint","IMPRINT",EDGE,{"derivedFrom":sQuery(id+"F16.wireOp",EDGE,"E87.MirrorCS")}),-1.0]])]});
            var Q1;
            {var subQ1=sQuery(id+"F16.wireOp",EDGE,"E79.1");Q1=makeQuery(id+"F16.imprint","IMPRINT",FACE,{"disambiguationData":[TD([[makeQuery(id+"F16.imprint","IMPRINT",EDGE,{"derivedFrom":subQ1}),1.0]])]});}
            var Q2;
            Q2=makeQuery(id+"F16.imprint","IMPRINT",FACE,{"disambiguationData":[TD([[makeQuery(id+"F16.imprint","IMPRINT",EDGE,{"derivedFrom":sQuery(id+"F16.wireOp",EDGE,"E81")}),-1.0]])]});
            var Q3;
            Q3=makeQuery(id+"F2.opExtrude","CAP_FACE",FACE,{"disambiguationData":[OSD([sQuery(id+"F0.wireOp",EDGE,"E12"),sQuery(id+"F0.wireOp",EDGE,"E13"),sQuery(id+"F0.wireOp",EDGE,"E14"),sQuery(id+"F0.wireOp",EDGE,"E15"),sQuery(id+"F0.wireOp",EDGE,"E17.filletArc"),sQuery(id+"F0.wireOp",EDGE,"E18.filletArc"),sQuery(id+"F0.wireOp",EDGE,"E19.filletArc"),sQuery(id+"F0.wireOp",EDGE,"E20.filletArc"),sQuery(id+"F0.wireOp",EDGE,"E25.0"),sQuery(id+"F0.wireOp",EDGE,"E25.1"),sQuery(id+"F0.wireOp",EDGE,"E25.2"),sQuery(id+"F0.wireOp",EDGE,"E25.3"),sQuery(id+"F0.wireOp",EDGE,"E25.4"),sQuery(id+"F0.wireOp",EDGE,"E25.5"),sQuery(id+"F0.wireOp",EDGE,"E25.6"),sQuery(id+"F0.wireOp",EDGE,"E25.7")])],"isStart":false});
            extrude(context, id + "F17", {"entities" : qUnion([Q0, Q1, Q2]), "operationType" : NewBodyOperationType.ADD, "endBound" : BoundingType.UP_TO_SURFACE, "endBoundEntityFace" : qUnion([Q3]), "depth" : 25 * mm});
        }
    });
